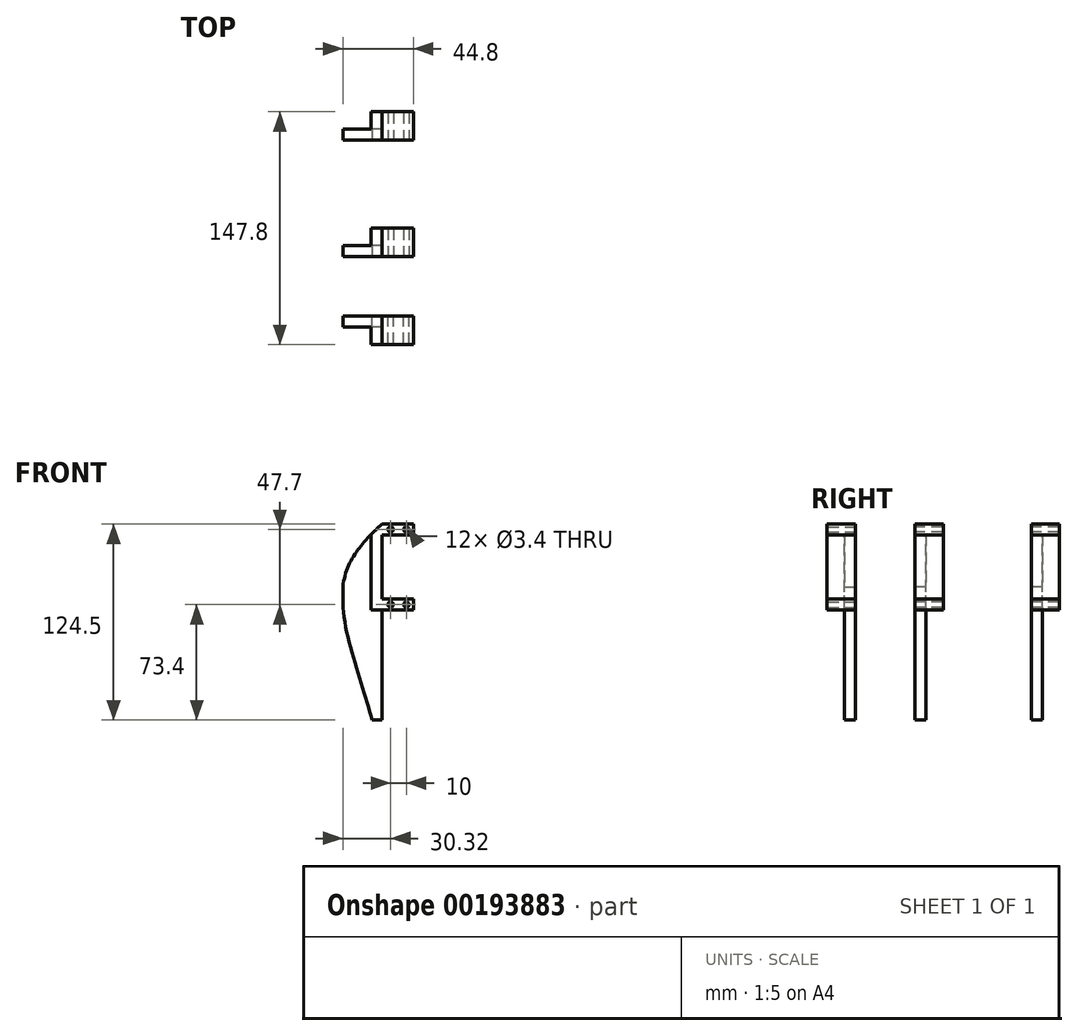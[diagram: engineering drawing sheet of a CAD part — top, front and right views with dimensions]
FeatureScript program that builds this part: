
annotation { "Feature Type Name" : "Feature", "Feature Type Description" : "" }
export const myFeature = defineFeature(function(context is Context, id is Id, definition is map)
    precondition{}
    {
        {
            var Q0;
            Q0=qCreatedBy(makeId("Front.planeOp"),FACE);
            var sketch = newSketch(context, id + "F0", { "sketchPlane" : qUnion([Q0])});
            skLineSegment(sketch, "E0.bottom", {"start": v(13.4, -27.25) * mm, "end": v(-13.4, -27.25) * mm});
            skLineSegment(sketch, "E0.top", {"start": v(13.4, 27.25) * mm, "end": v(-13.4, 27.25) * mm});
            skLineSegment(sketch, "E0.left", {"start": v(13.4, -27.25) * mm, "end": v(13.4, 27.25) * mm});
            skLineSegment(sketch, "E0.right", {"start": v(-13.4, -27.25) * mm, "end": v(-13.4, 27.25) * mm});
            skPoint(sketch, "E0.middle", {"position": v(0, 0) * mm});
            skSolve(sketch);
        }
        {
            var Q0;
            Q0 = qSketchRegion(id + "F0", true);
            extrude(context, id + "F1", {"entities" : qUnion([Q0]), "depth" : 18 * mm});
        }
        {
            var Q0;
            Q0=makeQuery(id+"F1.opExtrude","CAP_FACE",FACE,{"disambiguationData":[OSD([sQuery(id+"F0.wireOp",EDGE,"E0.bottom"),sQuery(id+"F0.wireOp",EDGE,"E0.top"),sQuery(id+"F0.wireOp",EDGE,"E0.left"),sQuery(id+"F0.wireOp",EDGE,"E0.right")])],"isStart":false});
            var sketch = newSketch(context, id + "F2", { "sketchPlane" : qUnion([Q0])});
            skLineSegment(sketch, "E1.bottom", {"start": v(13.4, 20.45) * mm, "end": v(-6.6, 20.45) * mm});
            skLineSegment(sketch, "E1.top", {"start": v(13.4, -20.45) * mm, "end": v(-6.6, -20.45) * mm});
            skLineSegment(sketch, "E1.left", {"start": v(13.4, 20.45) * mm, "end": v(13.4, -20.45) * mm});
            skLineSegment(sketch, "E1.right", {"start": v(-6.6, 20.45) * mm, "end": v(-6.6, -20.45) * mm});
            skSolve(sketch);
        }
        {
            var Q0;
            Q0 = qSketchRegion(id + "F2", true);
            extrude(context, id + "F3", {"entities" : qUnion([Q0]), "operationType" : NewBodyOperationType.REMOVE, "endBound" : BoundingType.THROUGH_ALL, "oppositeDirection" : true, "depth" : 25 * mm});
        }
        {
            var Q0;
            Q0=makeQuery(id+"F1.opExtrude","CAP_FACE",FACE,{"disambiguationData":[OSD([sQuery(id+"F0.wireOp",EDGE,"E0.bottom"),sQuery(id+"F0.wireOp",EDGE,"E0.top"),sQuery(id+"F0.wireOp",EDGE,"E0.left"),sQuery(id+"F0.wireOp",EDGE,"E0.right")])],"isStart":false});
            var sketch = newSketch(context, id + "F4", { "sketchPlane" : qUnion([Q0])});
            skCircle(sketch, "E2", {"center": v(8.92, 23.85) * mm, "radius": 1.7 * mm});
            skCircle(sketch, "E3", {"center": v(-1.08, 23.85) * mm, "radius": 1.7 * mm});
            skCircle(sketch, "E4.MirrorC", {"center": v(-1.08, -23.85) * mm, "radius": 1.7 * mm});
            skCircle(sketch, "E5.MirrorC", {"center": v(8.92, -23.85) * mm, "radius": 1.7 * mm});
            skSolve(sketch);
        }
        {
            var Q0;
            Q0 = qSketchRegion(id + "F4", true);
            extrude(context, id + "F5", {"entities" : qUnion([Q0]), "operationType" : NewBodyOperationType.REMOVE, "endBound" : BoundingType.THROUGH_ALL, "oppositeDirection" : true, "depth" : 25 * mm});
        }
        {
            var Q0;
            Q0=makeQuery(id+"F1.opExtrude","SWEPT_FACE",FACE,{"disambiguationData":[OSD([sQuery(id+"F0.wireOp",EDGE,"E0.bottom")])]});
            var sketch = newSketch(context, id + "F6", { "sketchPlane" : qUnion([Q0])});
            skLineSegment(sketch, "E6.bottom", {"start": v(-13.4, 18) * mm, "end": v(-6.6, 18) * mm});
            skLineSegment(sketch, "E6.top", {"start": v(-13.4, 0) * mm, "end": v(-6.6, 0) * mm});
            skLineSegment(sketch, "E6.left", {"start": v(-13.4, 18) * mm, "end": v(-13.4, 0) * mm});
            skLineSegment(sketch, "E6.right", {"start": v(-6.6, 18) * mm, "end": v(-6.6, 0) * mm});
            skSolve(sketch);
        }
        {
            var Q0;
            Q0 = qSketchRegion(id + "F6", true);
            extrude(context, id + "F7", {"entities" : qUnion([Q0]), "operationType" : NewBodyOperationType.ADD, "depth" : 70 * mm});
        }
        {
            var Q0;
            Q0=makeQuery(id+"F7.boolean.opBoolean","MERGE",FACE,{"derivedFrom":[makeQuery(id+"F1.opExtrude","SWEPT_FACE",FACE,{"disambiguationData":[OSD([sQuery(id+"F0.wireOp",EDGE,"E0.right")])]}),makeQuery(id+"F7.opExtrude","SWEPT_FACE",FACE,{"disambiguationData":[OSD([sQuery(id+"F6.wireOp",EDGE,"E6.left")])]})]});
            var sketch = newSketch(context, id + "F8", { "sketchPlane" : qUnion([Q0])});
            skPoint(sketch, "E7.0", {"position": v(18, -27.25) * mm});
            skLineSegment(sketch, "E8.bottom", {"start": v(0, -97.25) * mm, "end": v(11, -97.25) * mm});
            skLineSegment(sketch, "E8.top", {"start": v(0, -27.25) * mm, "end": v(11, -27.25) * mm});
            skLineSegment(sketch, "E8.left", {"start": v(0, -97.25) * mm, "end": v(0, -27.25) * mm});
            skLineSegment(sketch, "E8.right", {"start": v(11, -97.25) * mm, "end": v(11, -27.25) * mm});
            skSolve(sketch);
        }
        {
            var Q0;
            Q0 = qSketchRegion(id + "F8", true);
            extrude(context, id + "F9", {"entities" : qUnion([Q0]), "operationType" : NewBodyOperationType.REMOVE, "endBound" : BoundingType.THROUGH_ALL, "oppositeDirection" : true, "depth" : 25 * mm});
        }
        {
            var Q0;
            Q0=makeQuery(id+"F7.boolean.opBoolean","MERGE",FACE,{"derivedFrom":[makeQuery(id+"F1.opExtrude","SWEPT_FACE",FACE,{"disambiguationData":[OSD([sQuery(id+"F0.wireOp",EDGE,"E0.right")])]}),makeQuery(id+"F7.opExtrude","SWEPT_FACE",FACE,{"disambiguationData":[OSD([sQuery(id+"F6.wireOp",EDGE,"E6.left")])]})]});
            var sketch = newSketch(context, id + "F10", { "sketchPlane" : qUnion([Q0])});
            skLineSegment(sketch, "E9.bottom", {"start": v(11, -97.25) * mm, "end": v(18, -97.25) * mm});
            skLineSegment(sketch, "E9.top", {"start": v(11, 27.25) * mm, "end": v(18, 27.25) * mm});
            skLineSegment(sketch, "E9.left", {"start": v(11, -97.25) * mm, "end": v(11, 27.25) * mm});
            skLineSegment(sketch, "E9.right", {"start": v(18, -97.25) * mm, "end": v(18, 27.25) * mm});
            skSolve(sketch);
        }
        {
            var Q0;
            Q0 = qSketchRegion(id + "F10", true);
            extrude(context, id + "F11", {"entities" : qUnion([Q0]), "operationType" : NewBodyOperationType.ADD, "depth" : 18 * mm});
        }
        {
            var Q0;
            Q0=makeQuery(id+"F11.boolean.opBoolean","MERGE",FACE,{"derivedFrom":[makeQuery(id+"F7.boolean.opBoolean","MERGE",FACE,{"derivedFrom":[makeQuery(id+"F1.opExtrude","CAP_FACE",FACE,{"disambiguationData":[OSD([sQuery(id+"F0.wireOp",EDGE,"E0.bottom"),sQuery(id+"F0.wireOp",EDGE,"E0.top"),sQuery(id+"F0.wireOp",EDGE,"E0.left"),sQuery(id+"F0.wireOp",EDGE,"E0.right")])],"isStart":false}),makeQuery(id+"F7.opExtrude","SWEPT_FACE",FACE,{"disambiguationData":[OSD([sQuery(id+"F6.wireOp",EDGE,"E6.bottom")])]})]}),makeQuery(id+"F11.opExtrude","SWEPT_FACE",FACE,{"disambiguationData":[OSD([sQuery(id+"F10.wireOp",EDGE,"E9.right")])]})]});
            var sketch = newSketch(context, id + "F12", { "sketchPlane" : qUnion([Q0])});
            skFitSpline(sketch, "E10", {"points": [v(-6.6, 27.25) * mm, v(-31.4, -12.64) * mm, v(-12.77, -97.25) * mm], "startDerivative": vector(-79.75, -73.12) * mm, "endDerivative": vector(33.64, -128.86) * mm});
            skLineSegment(sketch, "E11", {"start": v(-6.6, 27.25) * mm, "end": v(-31.4, 27.25) * mm});
            skLineSegment(sketch, "E12", {"start": v(-31.4, 27.25) * mm, "end": v(-31.4, -12.64) * mm});
            skLineSegment(sketch, "E13", {"start": v(-31.4, -12.64) * mm, "end": v(-31.4, -97.25) * mm});
            skLineSegment(sketch, "E14", {"start": v(-31.4, -97.25) * mm, "end": v(-12.77, -97.25) * mm});
            skSolve(sketch);
        }
        {
            var Q0;
            Q0 = qSketchRegion(id + "F12", true);
            extrude(context, id + "F13", {"entities" : qUnion([Q0]), "operationType" : NewBodyOperationType.REMOVE, "endBound" : BoundingType.THROUGH_ALL, "oppositeDirection" : true, "depth" : 25 * mm});
        }
        {
            var Q0;
            Q0=makeQuery(id+"F1.opExtrude","SWEPT_BODY",BODY,{"disambiguationData":[OSD([sQuery(id+"F0.wireOp",EDGE,"E0.bottom"),sQuery(id+"F0.wireOp",EDGE,"E0.top"),sQuery(id+"F0.wireOp",EDGE,"E0.left"),sQuery(id+"F0.wireOp",EDGE,"E0.right")])]});
            transform(context, id + "F14", {"entities" : qUnion([Q0]), "transformType" : TransformType.TRANSLATION_3D, "dx" : 0 * mm, "dy" : 73.9 * mm, "dz" : 0 * mm, "makeCopy" : true});
        }
        {
            var Q0;
            Q0=makeQuery(id+"F14.opPattern","COPY",BODY,{"derivedFrom":makeQuery(id+"F1.opExtrude","SWEPT_BODY",BODY,{"disambiguationData":[OSD([sQuery(id+"F0.wireOp",EDGE,"E0.bottom"),sQuery(id+"F0.wireOp",EDGE,"E0.top"),sQuery(id+"F0.wireOp",EDGE,"E0.left"),sQuery(id+"F0.wireOp",EDGE,"E0.right")])]}),"instanceName":"1"});
            var Q1;
            Q1=qCreatedBy(makeId("Front.planeOp"),FACE);
            mirror(context, id + "F15", {"entities" : qUnion([Q0]), "mirrorPlane" : qUnion([Q1])});
        }
    });
